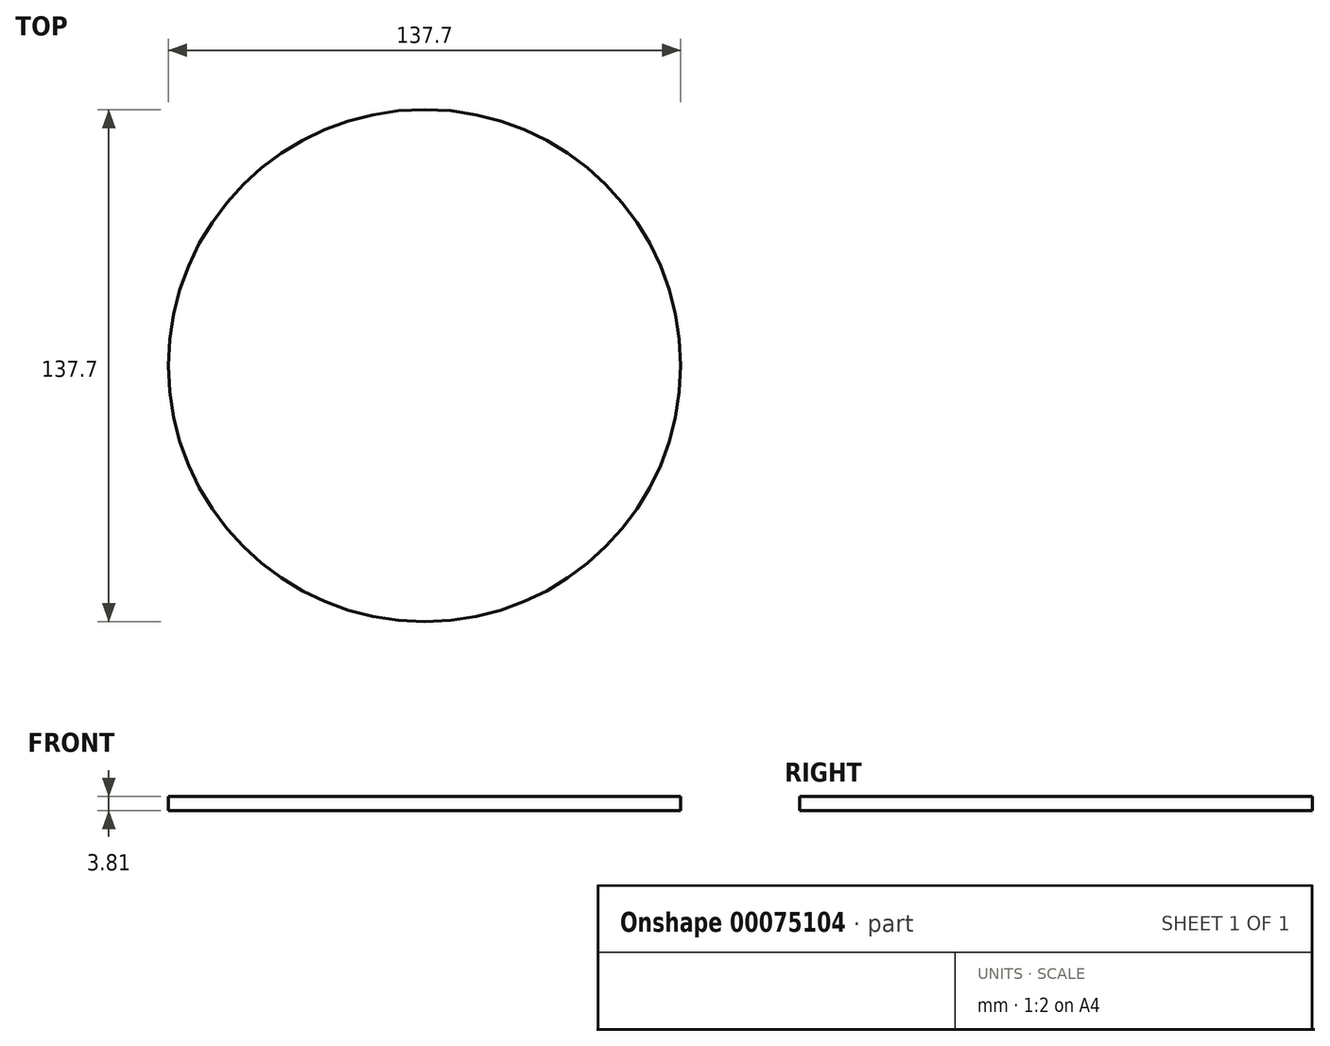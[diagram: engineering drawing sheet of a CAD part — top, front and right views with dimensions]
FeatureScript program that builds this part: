
annotation { "Feature Type Name" : "Feature", "Feature Type Description" : "" }
export const myFeature = defineFeature(function(context is Context, id is Id, definition is map)
    precondition{}
    {
        {
            var Q0;
            Q0=qCreatedBy(makeId("Top.planeOp"),FACE);
            var sketch = newSketch(context, id + "F0", { "sketchPlane" : qUnion([Q0])});
            skCircle(sketch, "E0", {"center": v(0, 0) * mm, "radius": 68.85 * mm});
            skSolve(sketch);
        }
        {
            var Q0;
            Q0=makeQuery(id+"F0.imprint","IMPRINT",FACE,{"disambiguationData":[TD([[makeQuery(id+"F0.imprint","IMPRINT",EDGE,{"derivedFrom":sQuery(id+"F0.wireOp",EDGE,"E0")}),1.0]])]});
            extrude(context, id + "F1", {"entities" : qUnion([Q0]), "depth" : 3.8 * mm});
        }
        {
            var Q0;
            Q0=qCreatedBy(makeId("Right.planeOp"),FACE);
            var sketch = newSketch(context, id + "F2", { "sketchPlane" : qUnion([Q0])});
            skArc(sketch, "E1", {"start": v(-68.06, 0) * mm, "mid": v(-0.23, -49.28) * mm, "end": v(67.6, 0) * mm});
            skSolve(sketch);
        }
    });
